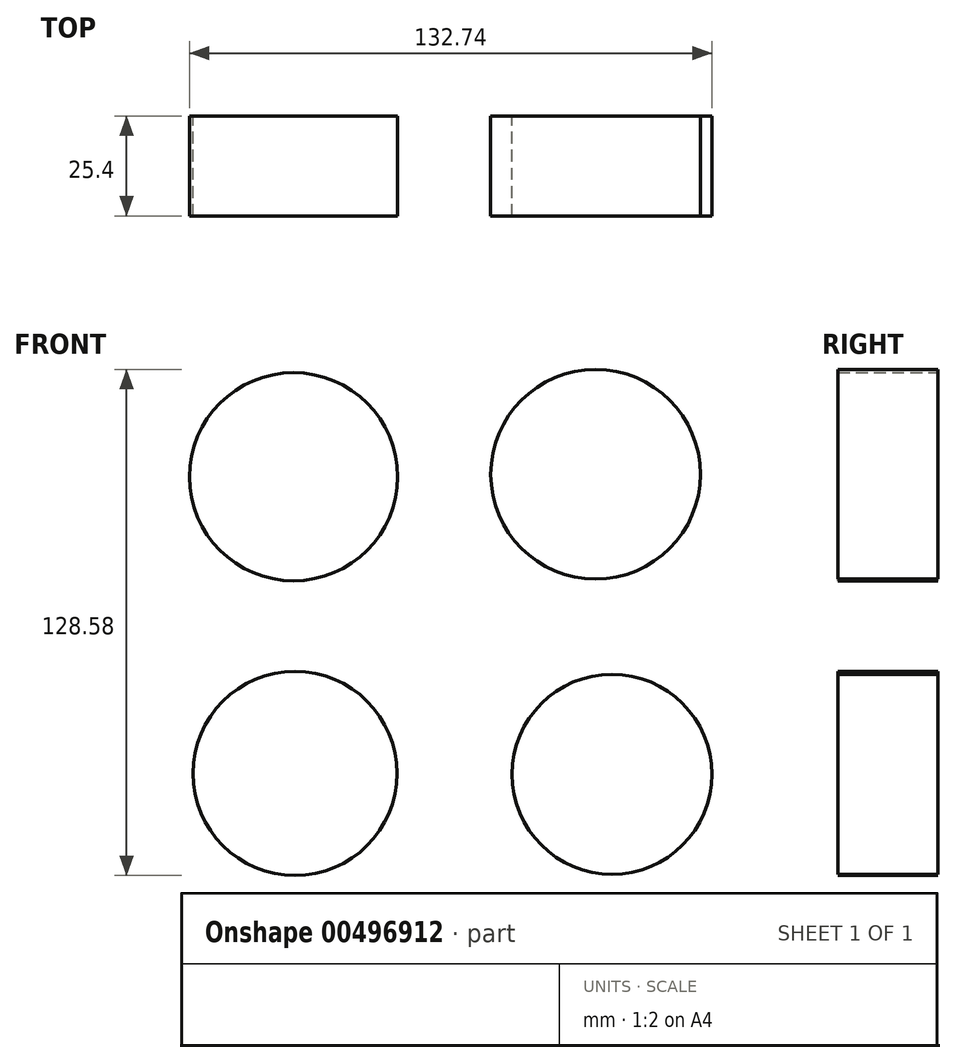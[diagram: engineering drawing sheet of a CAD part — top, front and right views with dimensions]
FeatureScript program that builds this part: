
annotation { "Feature Type Name" : "Feature", "Feature Type Description" : "" }
export const myFeature = defineFeature(function(context is Context, id is Id, definition is map)
    precondition{}
    {
        {
            var Q0;
            Q0=qCreatedBy(makeId("Front.planeOp"),FACE);
            var sketch = newSketch(context, id + "F0", { "sketchPlane" : qUnion([Q0])});
            skCircle(sketch, "E0", {"center": v(-40.35, 36.3) * mm, "radius": 26.44 * mm});
            skCircle(sketch, "E1", {"center": v(36.37, 36.93) * mm, "radius": 26.63 * mm});
            skCircle(sketch, "E2", {"center": v(-40, -39.07) * mm, "radius": 25.93 * mm});
            skCircle(sketch, "E3", {"center": v(40.55, -39.3) * mm, "radius": 25.4 * mm});
            skSolve(sketch);
        }
        {
            var Q0;
            Q0 = qSketchRegion(id + "F0", true);
            extrude(context, id + "F1", {"entities" : qUnion([Q0]), "depth" : 12.7 * mm, "hasSecondDirection" : true, "secondDirectionOppositeDirection" : true, "secondDirectionDepth" : 12.7 * mm});
        }
    });
